# Revit family: Spot Light - Exterior
name_source: partatom
category: Lighting Fixtures
revit_build: Autodesk Revit Architecture 2012 (Build: 20110210_1515)
units: mm (PartAtom-declared; Revit-internal decimal feet)

## types (4) — shared parameters
Assembly Code = D5020230
Ballast Number of Poles = 1
Color Filter = 16777215
Dimming Lamp Color Temperature Shift = <None>
Light Source Symbol Length = 10' - 0"
Load Classification = Lighting - Dwelling Unit
Spot Beam Angle = 30.00°
Spot Field Angle = 90.00°
Stand = Metal - Paint Finish - Ivory, Glossy
Tilt Angle = 60.00°

## per-type parameters (varying)
| type | Apparent Load | Ballast Voltage | Lamp | Shade | Wattage Comments |
| 300W Incandescent - 120V | 300 VA | 120 V | PS-30 | Metal - Paint Finish - Ivory, Glossy | 300 |
| 175W Metal Halide - 120V | 175 VA | 120 V | BT-28 | Metal - Paint Finish - Dark Gray, Matte | 175 |
| 175W Metal Halide - 277V | 175 VA | 277 V | BT-28 | Metal - Paint Finish - Dark Gray, Matte | 175 |
| 300W Incandescent - 277V | 300 VA | 277 V | PS-30 | Metal - Paint Finish - Ivory, Glossy | 300 |

## geometry (parser evidence)
native form markers: Sweep x1
no freeform markers — native parametric forms only
